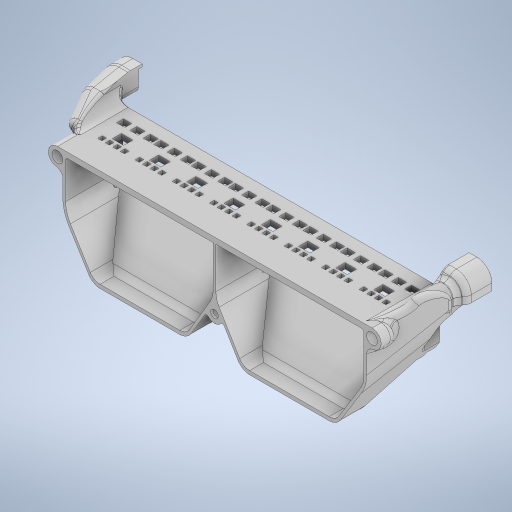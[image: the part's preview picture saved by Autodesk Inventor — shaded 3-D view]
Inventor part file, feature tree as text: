
AUTODESK INVENTOR PART (.ipt)
format: ipt  version: 2023.1 (Build 271208000, 208)  size: 8,087,552 bytes
history: native  units: mm
features: delete_face x74, projected_geometry x69, reference x62, sketch x58, extrude x56, fillet x51, other x19, chamfer x18, move_body x14, direct_edit x12, hole x3, plane x2
ambient origin geometry x8: Origin, YZ Plane, XZ Plane, XY Plane, X Axis, Y Axis, Z Axis, Center Point
bodies: Volumenkörper1 (feature_tree)
feature tree (438):
  extrude  "Extrusion1"  Depth=2.6mm
  extrude  "Extrusion2"  Depth=0.4195mm
  extrude  "Extrusion3"  Depth=8.0mm
  extrude  "Extrusion4"  Depth=2.6mm
  extrude  "Extrusion5"  Depth=0.482959mm
  extrude  "Extrusion6"  Depth=0.4mm
  delete_face  "Fläche löschen1"
  extrude  "Extrusion7"  Depth=9.8mm TaperAngle=0.0deg
  extrude  "Extrusion8"  Depth=3.0mm TaperAngle=0.0deg
  extrude  "Extrusion9"  Depth=40.0mm
  delete_face  "Fläche löschen2"
  delete_face  "Fläche löschen3"
  delete_face  "Fläche löschen4"
  extrude  "Extrusion10"  Depth=40.0mm
  delete_face  "Fläche löschen5"
  delete_face  "Fläche löschen6"
  delete_face  "Fläche löschen7"
  extrude  "Extrusion11"  Depth=12.004mm
  delete_face  "Fläche löschen8"
  extrude  "Extrusion12"  Depth=12.131mm
  delete_face  "Fläche löschen9"
  delete_face  "Fläche löschen10"
  delete_face  "Fläche löschen11"
  delete_face  "Fläche löschen12"
  extrude  "Extrusion13"  Depth=2.0mm
  extrude  "Extrusion14"  Depth=12.0mm TaperAngle=0.0deg
  delete_face  "Fläche löschen13"
  direct_edit  "Direktbearbeitung1"
  extrude  "Extrusion15"  Depth=0.2mm
  extrude  "Extrusion16"  Depth=0.2mm
  chamfer  "Fase1"  Distance=12.0mm
  delete_face  "Fläche löschen14"
  delete_face  "Fläche löschen15"
  chamfer  "Fase2"  Distance=10.0mm
  delete_face  "Fläche löschen16"
  chamfer  "Fase3"  Distance=10.0mm
  chamfer  "Fase4"  [1 undecoded]
  extrude  "Extrusion17"  Depth=10.0mm TaperAngle=0.0deg
  extrude  "Extrusion18"  Depth=1.2mm
  delete_face  "Fläche löschen17"
  extrude  "Extrusion19"  Depth=54.3755mm
  delete_face  "Fläche löschen18"
  delete_face  "Fläche löschen19"
  extrude  "Extrusion20"  Depth=10.0mm TaperAngle=0.0deg
  extrude  "Extrusion21"  Depth=10.0mm
  fillet  "Rundung1"  Radius=2.044525mm
  fillet  "Rundung2"  Radius=2.044525mm
  delete_face  "Fläche löschen20"
  delete_face  "Fläche löschen21"
  extrude  "Extrusion22"  Depth=10.0mm TaperAngle=0.0deg
  delete_face  "Fläche löschen22"
  extrude  "Extrusion23"  Depth=40.4mm
  extrude  "Extrusion24"  Depth=40.4mm
  delete_face  "Fläche löschen23"
  extrude  "Extrusion25"  Depth=2.391982mm
  delete_face  "Fläche löschen24"
  extrude  "Extrusion26"  Depth=20.0mm
  delete_face  "Fläche löschen25"
  extrude  "Extrusion27"  TaperAngle=30.0deg  [1 undecoded]
  delete_face  "Fläche löschen26"
  direct_edit  "Direktbearbeitung2"
  extrude  "Extrusion28"  Depth=40.6558mm
  extrude  "Extrusion29"  Depth=4.1mm
  extrude  "Extrusion30"  Depth=4.1mm
  extrude  "Extrusion31"  Depth=11.1mm
  extrude  "Extrusion32"  Depth=12.3mm
  extrude  "Extrusion33"  Depth=16.4mm
  direct_edit  "Direktbearbeitung3"
  delete_face  "Fläche löschen27"
  extrude  "Extrusion34"  Depth=8.2mm
  delete_face  "Fläche löschen28"
  delete_face  "Fläche löschen29"
  delete_face  "Fläche löschen30"
  delete_face  "Fläche löschen31"
  fillet  "Rundung3"  Radius=7.0mm
  extrude  "Extrusion35"  Depth=1.2mm
  chamfer  "Fase5"  Distance=19.7279mm
  extrude  "Extrusion36"  Depth=3.0mm
  delete_face  "Fläche löschen32"
  delete_face  "Fläche löschen33"
  direct_edit  "Direktbearbeitung4"
  extrude  "Extrusion37"  Depth=3.0mm
  fillet  "Rundung4"  Radius=11.1mm
  fillet  "Rundung5"  Radius=4.1mm
  fillet  "Rundung6"  Radius=2.9mm
  fillet  "Rundung7"  Radius=4.1mm
  fillet  "Rundung8"  Radius=5.3mm
  fillet  "Rundung9"  Radius=12.3mm
  chamfer  "Fase7"  Distance=13.5mm
  extrude  "Extrusion38"  Depth=3.0mm
  sketch  "Skizze44"  dims[d78=10.0mm d79=0.0mm d80=10.0mm d81=0.0mm]
  extrude  "Extrusion39"  Depth=3.0mm
  extrude  "Extrusion40"  Depth=3.0mm
  direct_edit  "Direktbearbeitung5"
  chamfer  "Fase8"  Distance=15.2mm
  fillet  "Rundung10"  Radius=8.2mm
  delete_face  "Fläche löschen34"
  delete_face  "Fläche löschen35"
  fillet  "Rundung11"  Radius=7.0mm
  fillet  "Rundung12"  Radius=0.0mm
  extrude  "Extrusion41"  Depth=3.0mm
  extrude  "Extrusion42"  Depth=3.0mm
  direct_edit  "Direktbearbeitung6"
  hole  "Bohrung1"  [1 undecoded]
  direct_edit  "Direktbearbeitung7"
  extrude  "Extrusion43"  Depth=3.0mm
  fillet  "Rundung13"  Radius=17.6mm
  extrude  "Extrusion44"  Depth=3.0mm
  plane  "Arbeitsebene4"
  other  "Trennen2"
  fillet  "Rundung14"  Radius=13.5mm
  delete_face  "Fläche löschen37"
  fillet  "Rundung15"  Radius=11.1mm
  fillet  "Rundung16"  Radius=12.3mm
  extrude  "Extrusion45"  Depth=3.0mm
  hole  "Bohrung2"  [1 undecoded]
  fillet  "Rundung17"  Radius=4.1mm
  extrude  "Extrusion46"  Depth=3.0mm
  delete_face  "Fläche löschen38"
  fillet  "Rundung18"  Radius=0.0mm
  fillet  "Rundung19"  Radius=1.2mm
  fillet  "Rundung20"  Radius=4.1mm
  delete_face  "Fläche löschen39"
  fillet  "Rundung21"  Radius=2.9mm
  delete_face  "Fläche löschen40"
  fillet  "Rundung22"  Radius=1.2mm
  fillet  "Rundung23"  Radius=5.3mm
  fillet  "Rundung24"  Radius=0.0mm
  fillet  "Rundung25"  Radius=4.1mm
  delete_face  "Fläche löschen41"
  chamfer  "Fase9"  Distance=8.2mm
  delete_face  "Fläche löschen42"
  fillet  "Rundung26"  Radius=12.3mm
  delete_face  "Fläche löschen43"
  extrude  "Extrusion47"  Depth=3.0mm
  delete_face  "Fläche löschen44"
  delete_face  "Fläche löschen45"
  extrude  "Extrusion48"  Depth=3.0mm
  delete_face  "Fläche löschen46"
  chamfer  "Fase10"  Distance=5.3mm
  fillet  "Rundung27"  Radius=9.4mm
  fillet  "Rundung28"  Radius=13.5mm
  fillet  "Rundung29"  Radius=17.6mm
  delete_face  "Fläche löschen47"
  chamfer  "Fase11"  Distance=4.1mm
  delete_face  "Fläche löschen48"
  chamfer  "Fase12"  Distance=8.2mm
  extrude  "Extrusion49"  Depth=3.0mm
  fillet  "Rundung30"  Radius=16.4mm
  extrude  "Extrusion50"  Depth=3.0mm
  fillet  "Rundung31"  Radius=5.3mm
  fillet  "Rundung32"  Radius=9.4mm
  delete_face  "Fläche löschen49"
  delete_face  "Fläche löschen50"
  direct_edit  "Direktbearbeitung8"
  extrude  "Extrusion51"  Depth=3.0mm
  delete_face  "Fläche löschen51"
  delete_face  "Fläche löschen52"
  extrude  "Extrusion52"  Depth=3.0mm
  delete_face  "Fläche löschen53"
  delete_face  "Fläche löschen54"
  delete_face  "Fläche löschen55"
  delete_face  "Fläche löschen56"
  direct_edit  "Direktbearbeitung9"
  fillet  "Rundung40"  Radius=21.7mm
  chamfer  "Fase13"  Distance=12.3mm
  chamfer  "Fase14"  Distance=16.4mm
  chamfer  "Fase15"  Distance=20.5mm
  fillet  "Rundung41"  Radius=24.6mm
  fillet  "Rundung42"  Radius=28.7mm
  delete_face  "Fläche löschen57"
  direct_edit  "Direktbearbeitung10"
  delete_face  "Fläche löschen58"
  fillet  "Rundung43"  Radius=13.5mm
  fillet  "Rundung44"  Radius=17.6mm
  delete_face  "Fläche löschen59"
  fillet  "Rundung45"  Radius=21.7mm
  delete_face  "Fläche löschen60"
  fillet  "Rundung46"  Radius=25.8mm
  delete_face  "Fläche löschen61"
  delete_face  "Fläche löschen62"
  delete_face  "Fläche löschen63"
  hole  "Bohrung3"  [1 undecoded]
  fillet  "Rundung47"  Radius=16.4mm
  fillet  "Rundung48"  Radius=20.5mm
  fillet  "Rundung49"  Radius=24.6mm
  fillet  "Rundung50"  Radius=28.7mm
  delete_face  "Fläche löschen64"
  plane  "Arbeitsebene5"
  extrude  "Extrusion53"  Depth=3.0mm
  direct_edit  "Direktbearbeitung11"
  fillet  "Rundung51"  Radius=17.6mm
  chamfer  "Fase16"  Distance=21.7mm
  delete_face  "Fläche löschen65"
  delete_face  "Fläche löschen66"
  extrude  "Extrusion54"  Depth=3.0mm
  delete_face  "Fläche löschen67"
  fillet  "Rundung52"  Radius=29.9mm
  extrude  "Extrusion55"  Depth=3.0mm
  fillet  "Rundung53"  Radius=28.7mm
  delete_face  "Fläche löschen68"
  extrude  "Extrusion56"  Depth=3.0mm
  fillet  "Rundung54"  Radius=36.9mm
  fillet  "Rundung55"  Radius=29.9mm
  chamfer  "Fase17"  Distance=34.0mm
  delete_face  "Fläche löschen69"
  delete_face  "Fläche löschen70"
  delete_face  "Fläche löschen71"
  direct_edit  "Direktbearbeitung12"
  delete_face  "Fläche löschen72"
  fillet  "Rundung56"  Radius=4.1mm
  chamfer  "Fase18"  Distance=1.2mm
  delete_face  "Fläche löschen73"
  chamfer  "Fase19"  Distance=2.9mm
  fillet  "Rundung57"  Radius=5.3mm
  fillet  "Rundung58"  Radius=12.3mm
  delete_face  "Fläche löschen74"
  delete_face  "Fläche löschen75"
  sketch  "Skizze1"  dims[d0=8.8mm d1=0.0mm d4=2.6mm]
  reference  "Referenz1"
  reference  "Referenz2"
  reference  "Referenz3"
  reference  "Referenz4"
  reference  "Referenz5"
  reference  "Referenz6"
  reference  "Referenz7"
  reference  "Referenz8"
  reference  "Referenz9"
  reference  "Referenz10"
  reference  "Referenz11"
  reference  "Referenz12"
  reference  "Referenz13"
  sketch  "Skizze2"  dims[d5=0.4195mm d6=0.4195mm]
  reference  "Referenz14"
  reference  "Referenz15"
  projected_geometry  "Projizierte Kontur1"
  reference  "Referenz16"
  reference  "Referenz17"
  reference  "Referenz18"
  reference  "Referenz19"
  sketch  "Skizze3"  dims[d7=5.999988mm d8=8.0mm]
  projected_geometry  "Projizierte Kontur2"
  reference  "Referenz20"
  reference  "Referenz21"
  reference  "Referenz22"
  reference  "Referenz23"
  reference  "Referenz24"
  reference  "Referenz25"
  sketch  "Skizze4"  dims[d9=8.0mm d10=2.6mm]
  projected_geometry  "Projizierte Kontur3"
  reference  "Referenz26"
  reference  "Referenz27"
  reference  "Referenz28"
  reference  "Referenz29"
  sketch  "Skizze5"  dims[d11=0.482959mm d12=0.482959mm]
  projected_geometry  "Projizierte Kontur4"
  projected_geometry  "Projizierte Kontur5"
  projected_geometry  "Projizierte Kontur6"
  projected_geometry  "Projizierte Kontur7"
  sketch  "Skizze7"  dims[d13=0.4mm d14=0.4mm]
  projected_geometry  "Projizierte Kontur8"
  reference  "Referenz30"
  reference  "Referenz31"
  sketch  "Skizze9"  dims[d15=2.6mm d16=9.8mm d17=0.0mm]
  projected_geometry  "Projizierte Kontur9"
  reference  "Referenz34"
  reference  "Referenz35"
  reference  "Referenz36"
  sketch  "Skizze10"  dims[d18=0.4mm d19=3.0mm d20=0.0mm]
  projected_geometry  "Projizierte Kontur10"
  projected_geometry  "Projizierte Kontur11"
  sketch  "Skizze11"  dims[d21=40.0mm d22=40.0mm]
  projected_geometry  "Projizierte Kontur12"
  sketch  "Skizze13"  dims[d23=40.0mm d24=40.0mm]
  projected_geometry  "Projizierte Kontur13"
  sketch  "Skizze14"  dims[d25=12.004mm d26=12.004mm]
  projected_geometry  "Projizierte Kontur14"
  reference  "Referenz37"
  reference  "Referenz38"
  reference  "Referenz39"
  reference  "Referenz40"
  sketch  "Skizze15"  dims[d27=12.131mm d28=12.131mm]
  projected_geometry  "Projizierte Kontur15"
  sketch  "Skizze16"  dims[d29=2.0mm d30=0.492mm]
  projected_geometry  "Projizierte Kontur16"
  projected_geometry  "Projizierte Kontur17"
  sketch  "Skizze17"  dims[d31=0.492mm d32=12.0mm d33=0.0mm]
  projected_geometry  "Projizierte Kontur18"
  reference  "Referenz41"
  reference  "Referenz42"
  reference  "Referenz43"
  reference  "Referenz44"
  reference  "Referenz45"
  sketch  "Skizze18"  dims[d34=0.2mm d35=0.2mm]
  projected_geometry  "Projizierte Kontur19"
  sketch  "Skizze20"  dims[d36=0.2mm d37=0.2mm]
  projected_geometry  "Projizierte Kontur20"
  projected_geometry  "Projizierte Kontur21"
  sketch  "Skizze21"  dims[d38=0.2mm]
  sketch  "Skizze22"  dims[d39=0.2mm]
  projected_geometry  "Projizierte Kontur22"
  projected_geometry  "Projizierte Kontur23"
  sketch  "Skizze23"  dims[d40=0.2mm]
  sketch  "Skizze24"  dims[d41=1.6mm]
  projected_geometry  "Projizierte Kontur24"
  sketch  "Skizze25"  dims[d42=1.6mm]
  projected_geometry  "Projizierte Kontur25"
  projected_geometry  "Projizierte Kontur26"
  sketch  "Skizze27"  dims[d43=1.6mm]
  projected_geometry  "Projizierte Kontur28"
  sketch  "Skizze28"  dims[d44=1.6mm]
  projected_geometry  "Projizierte Kontur29"
  projected_geometry  "Projizierte Kontur30"
  projected_geometry  "Projizierte Kontur31"
  sketch  "Skizze29"  dims[d45=1.6mm]
  projected_geometry  "Projizierte Kontur32"
  sketch  "Skizze30"  dims[d46=1.6mm]
  projected_geometry  "Projizierte Kontur33"
  sketch  "Skizze31"  dims[d47=1.6mm]
  projected_geometry  "Projizierte Kontur34"
  sketch  "Skizze32"  dims[d48=1.6mm d49=12.0mm d50=0.0mm]
  sketch  "Skizze33"  dims[d51=1.0mm]
  projected_geometry  "Projizierte Kontur35"
  sketch  "Skizze34"  dims[d52=4.2mm]
  projected_geometry  "Projizierte Kontur36"
  projected_geometry  "Projizierte Kontur37"
  sketch  "Skizze35"  dims[d53=1.2mm d54=10.0mm d55=0.0mm]
  projected_geometry  "Projizierte Kontur38"
  projected_geometry  "Projizierte Kontur39"
  sketch  "Skizze36"  dims[d61=1.6mm]
  projected_geometry  "Projizierte Kontur40"
  sketch  "Skizze37"  dims[d62=0.292mm]
  projected_geometry  "Projizierte Kontur41"
  projected_geometry  "Projizierte Kontur42"
  sketch  "Skizze38"  dims[d63=0.292mm]
  projected_geometry  "Projizierte Kontur43"
  sketch  "Skizze39"  dims[d64=1.2mm]
  projected_geometry  "Projizierte Kontur44"
  projected_geometry  "Projizierte Kontur45"
  sketch  "Skizze40"  dims[d65=1.2mm d66=10.0mm d67=0.0mm d68=0.0mm d69=0.0mm]
  projected_geometry  "Projizierte Kontur46"
  sketch  "Skizze41"  dims[d70=10.0mm d71=0.0mm d72=10.0mm d73=0.0mm]
  projected_geometry  "Projizierte Kontur47"
  sketch  "Skizze42"  dims[d74=0.0mm d75=1.2mm]
  projected_geometry  "Projizierte Kontur48"
  sketch  "Skizze43"  dims[d76=108.751mm d77=54.3755mm]
  projected_geometry  "Projizierte Kontur49"
  reference  "Referenz47"
  reference  "Referenz48"
  reference  "Referenz49"
  reference  "Referenz50"
  reference  "Referenz51"
  reference  "Referenz52"
  reference  "Referenz53"
  reference  "Referenz54"
  reference  "Referenz55"
  reference  "Referenz56"
  reference  "Referenz57"
  reference  "Referenz58"
  reference  "Referenz59"
  reference  "Referenz60"
  reference  "Referenz61"
  reference  "Referenz62"
  reference  "Referenz63"
  sketch  "Skizze45"  dims[d82=10.0mm d83=0.0mm d84=1.2mm d85=2.044525mm d86=2.044525mm]
  projected_geometry  "Projizierte Kontur50"
  projected_geometry  "Projizierte Kontur51"
  sketch  "Skizze46"  dims[d87=10.0mm d88=0.0mm d89=0.0mm d90=0.0mm d91=5.0mm]
  projected_geometry  "Projizierte Kontur52"
  sketch  "Skizze47"  dims[d92=12.0mm d93=0.0mm d94=40.4mm]
  reference  "Referenz64"
  reference  "Referenz65"
  sketch  "Skizze48"  dims[d95=40.4mm d97=40.4mm]
  sketch  "Skizze49"  dims[d98=0.0mm d99=2.391982mm]
  sketch  "Skizze50"  dims[d100=2.6mm d101=20.0mm]
  projected_geometry  "Projizierte Kontur53"
  sketch  "Skizze51"  dims[d102=30.0deg d103=30.0deg]
  projected_geometry  "Projizierte Kontur54"
  sketch  "Skizze52"  dims[d104=45.0deg d105=40.6558mm]
  projected_geometry  "Projizierte Kontur55"
  projected_geometry  "Projizierte Kontur56"
  projected_geometry  "Projizierte Kontur57"
  sketch  "Skizze53"  dims[d106=1.2mm d107=4.1mm]
  projected_geometry  "Projizierte Kontur58"
  projected_geometry  "Projizierte Kontur59"
  sketch  "Skizze54"  dims[d108=2.9mm d109=4.1mm]
  projected_geometry  "Projizierte Kontur60"
  projected_geometry  "Projizierte Kontur61"
  sketch  "Skizze55"  dims[d110=5.3mm d111=11.1mm]
  projected_geometry  "Projizierte Kontur62"
  sketch  "Skizze56"  dims[d112=12.3mm d113=12.3mm]
  projected_geometry  "Projizierte Kontur63"
  sketch  "Skizze57"  dims[d114=13.5mm d115=16.4mm]
  projected_geometry  "Projizierte Kontur64"
  projected_geometry  "Projizierte Kontur65"
  sketch  "Skizze58"  dims[d116=15.2mm d117=8.2mm d118=7.0mm]
  projected_geometry  "Projizierte Kontur66"
  sketch  "Skizze59"  dims[d119=0.0mm d120=1.2mm]
  projected_geometry  "Projizierte Kontur67"
  sketch  "Skizze60"  dims[d121=8.2mm]
  projected_geometry  "Projizierte Kontur68"
  sketch  "Skizze61"  dims[d122=9.4mm]
  projected_geometry  "Projizierte Kontur69"
  sketch  "Skizze62"  dims[d123=16.4mm]
  sketch  "Skizze63"  dims[d124=17.6mm d125=19.7279mm d126=19.3mm d127=12.3mm d128=11.1mm d129=4.1mm d130=2.9mm d131=4.1mm d132=5.3mm d133=12.3mm d134=13.5mm d135=20.5mm d136=20.9279mm d137=16.4mm d138=15.2mm d139=8.2mm d140=7.0mm d141=0.0mm d142=1.2mm d143=8.2mm d144=9.4mm d145=16.4mm d146=17.6mm d147=12.3mm d148=13.5mm d149=11.1mm d150=12.3mm d151=4.1mm d152=2.9mm d153=4.1mm d154=5.3mm d155=0.0mm d156=1.2mm d157=4.1mm d158=2.9mm d159=1.2mm d160=5.3mm d161=0.0mm d162=4.1mm d163=8.2mm d164=12.3mm d165=16.4mm d166=1.2mm d167=5.3mm d168=9.4mm d169=13.5mm d170=17.6mm d171=4.1mm d172=8.2mm d173=12.3mm d174=16.4mm d175=20.5mm d176=5.3mm d177=9.4mm d178=13.5mm d179=17.6mm d180=21.7mm d181=12.3mm d182=16.4mm d183=20.5mm d184=24.6mm d185=28.7mm d186=13.5mm d187=17.6mm d188=21.7mm d189=25.8mm d190=29.9mm d191=16.4mm d192=20.5mm d193=24.6mm d194=28.7mm d195=32.8mm d196=17.6mm d197=21.7mm d198=25.8mm d199=29.9mm d200=34.0mm d201=28.7mm d202=32.8mm d203=36.9mm d204=29.9mm d205=34.0mm d206=4.1mm d207=1.2mm d208=2.9mm d209=5.3mm d210=12.3mm d211=8.2mm d212=4.1mm d213=0.0mm d214=16.4mm d215=13.5mm d216=9.4mm d217=5.3mm d218=1.2mm d219=17.6mm d220=4.1mm d221=20.5mm d222=16.4mm d223=12.3mm d224=8.2mm d225=5.3mm d226=21.7mm d227=17.6mm d228=13.5mm d229=9.4mm d230=24.6mm d231=20.5mm d232=16.4mm d233=12.3mm d234=28.7mm d235=25.8mm d236=21.7mm d237=17.6mm d238=13.5mm d239=29.9mm d240=16.4mm d241=32.8mm d242=28.7mm d243=24.6mm d244=20.5mm d245=17.6mm d246=34.0mm d247=29.9mm d248=25.8mm d249=21.7mm d250=28.7mm d251=36.9mm d252=32.8mm d253=29.9mm d254=34.0mm d255=3.592392mm d256=0.0mm d257=3.592392mm d258=3.592392mm d259=0.0mm d260=3.592392mm d261=9.572437mm d262=8.363481mm d263=0.10481mm d264=25.260409mm d265=0.336902mm d266=0.336902mm d267=4.2624mm d268=15.4655mm d269=4.2624mm d270=16.6655mm d271=33.794072mm d272=33.794072mm d273=36.334277mm d274=36.334277mm d275=38.3558mm d276=18.6279mm d277=0.1279mm d278=0.1279mm d279=1.2mm d280=0.6mm d281=2.0mm d282=0.0mm d283=0.6mm d284=2.0mm d285=45.0deg d286=0.4mm d287=2.0mm d288=45.0deg d289=0.6mm d290=2.0mm d291=45.0deg d292=0.4mm d293=2.0mm d294=45.0deg d295=0.0mm d296=0.0mm d297=10.0mm d298=0.0mm d300=12.0mm d301=1.2mm d302=10.0mm d303=0.0mm d304=0.0mm d305=0.0mm d306=3.0mm d307=0.0mm d308=5.0mm d309=6.6mm d310=3.0mm d311=0.0mm d312=10.0mm d313=0.0mm d314=10.0mm d315=0.0mm d316=10.0mm d317=0.0mm d318=0.0mm d319=0.0mm d320=10.0mm d321=0.0mm d322=0.0mm d323=0.0mm d324=5.0mm d325=10.0mm d326=0.0mm d327=10.0mm d328=0.0mm d329=10.0mm d330=0.0mm d331=10.0mm d332=0.0mm d333=1.2mm d334=10.0mm d335=0.0mm d336=10.0mm d337=0.0mm d338=0.0mm d339=0.0mm d340=1.75mm d341=10.0mm d342=0.0mm d343=0.4mm d344=2.0mm d345=0.0mm d346=0.6mm d347=2.0mm d348=45.0deg d349=1.0mm d350=0.0mm d351=0.0mm d352=0.0mm d353=1.75mm d354=1.0mm d355=0.0mm d356=2.0mm d357=1.0mm d358=0.4mm d359=10.0mm d360=5.0mm d361=2.0mm d365=0.4mm d366=2.0mm d367=45.0deg d368=5.6mm d369=3.0mm d370=3.6mm d371=3.6mm d372=3.6mm d373=2.220006mm d374=2.220006mm d375=3.6mm d376=3.6mm d377=3.6mm d378=2.220006mm d379=2.220006mm d380=3.6mm d381=3.6mm d382=3.6mm d383=2.220006mm d384=2.220006mm d385=3.6mm d386=3.6mm d387=3.6mm d388=2.220006mm d389=2.220006mm d390=3.6mm d391=3.6mm d392=3.6mm d393=2.220006mm d394=2.220006mm d395=3.6mm d396=3.6mm d397=3.6mm d398=2.220006mm d399=2.220006mm d400=3.6mm d401=3.6mm d402=3.6mm d403=2.220006mm d404=2.220006mm d425=3.6mm d426=3.6mm d427=3.6mm d428=2.220006mm d429=2.220006mm d430=0.4mm d431=0.0mm d432=0.3mm d433=0.3mm d434=0.3mm d435=0.3mm d437=0.3mm d438=1.2mm d439=1.2mm d440=1.2mm d441=1.2mm d443=1.2mm d444=10.0mm d445=0.0mm d446=1.6mm d447=0.0mm d448=0.0mm d449=0.0mm d450=4.0mm d451=3.8mm d452=2.0mm d453=45.0deg d454=4.0mm d455=4.0mm d456=5.2mm d457=5.0mm d458=10.0mm d459=0.0mm d460=6.2mm d461=0.0mm d462=0.0mm d463=0.0mm d464=0.0mm d465=-1.0mm d466=3.3mm d467=6.0mm d468=4.7mm d469=5.0mm d470=90.0deg d471=8.0mm d472=20.594885mm d473=0.0mm d474=0.0mm d475=0.4mm d476=0.0mm d477=0.0mm d478=1.485505mm d479=0.0mm d480=0.0mm d481=1.000006mm d482=0.0mm d483=0.0mm d484=10.0mm d485=3.0mm d486=3.0mm d487=4.0mm d488=5.0mm d489=5.0mm d490=5.0mm d491=5.0mm d492=5.0mm d493=5.0mm d494=5.0mm d495=5.0mm d496=5.120006mm d497=5.120006mm d498=5.120006mm d499=5.120006mm d500=5.120006mm d501=5.120006mm d502=5.120006mm d503=5.120006mm d504=5.120006mm d505=5.120006mm d506=5.120006mm d507=5.120006mm d508=5.120006mm d509=5.120006mm d510=5.120006mm d511=5.120006mm d512=1.0mm d513=2.0mm d514=2.0mm d522=1.8mm d523=2.0mm d524=1.8mm d525=1.8mm d526=1.8mm d527=11.640012mm d528=11.640012mm d529=1.480004mm d530=1.480004mm d531=1.480004mm d532=1.8mm d533=2.0mm d534=1.8mm d535=1.8mm d536=1.8mm d537=11.640012mm d538=1.480004mm d539=1.480004mm d540=1.480004mm d541=2.0mm d542=11.640012mm d543=1.8mm d544=2.0mm d545=1.8mm d546=1.8mm d547=1.8mm d548=11.640012mm d549=1.480004mm d550=1.480004mm d551=1.480004mm d552=2.0mm d553=11.640012mm d554=1.8mm d555=2.0mm d556=1.8mm d557=1.8mm d558=1.8mm d559=11.640012mm d560=1.480004mm d561=1.480004mm d562=1.480004mm d563=2.0mm d564=11.640012mm d565=1.8mm d566=2.0mm d567=1.8mm d568=1.8mm d569=1.8mm d570=11.640012mm d571=1.480004mm d572=1.480004mm d573=1.480004mm d574=2.0mm d575=11.640012mm d576=1.8mm d577=2.0mm d578=1.8mm d579=1.8mm d580=1.8mm d581=11.640012mm d582=1.480004mm d583=1.480004mm d584=1.480004mm d585=2.0mm d586=11.640012mm d587=1.8mm d588=2.0mm d589=1.8mm d590=1.8mm d591=1.8mm d592=11.640012mm d593=1.480004mm d594=1.480004mm d595=1.480004mm d596=2.0mm d597=11.640012mm d598=1.8mm d599=2.0mm d600=1.8mm d601=1.8mm d602=1.8mm d603=11.640012mm d604=1.480004mm d605=1.480004mm d606=1.480004mm d607=2.0mm d608=11.640012mm d609=3.0mm d610=0.0mm d611=-6.0mm d612=10.0mm d613=10.0mm d614=14.0mm d615=4.7mm d616=6.0mm d617=0.0mm d618=3.3mm d619=6.0mm d620=4.7mm d621=5.0mm d622=90.0deg d623=8.0mm d624=20.594885mm d625=1.0mm d626=1.2mm d627=1.2mm d628=0.0mm d629=0.0mm d630=10.0mm d631=10.0mm d632=5.0mm d633=1.0mm d634=1.0mm d635=10.0mm d636=10.0mm d637=3.0mm d638=0.4mm d639=2.0mm d640=45.0deg d641=2.0mm d642=10.0mm d643=0.0mm d644=10.0mm d645=0.0mm d646=0.4mm d647=2.0mm d648=45.0deg d649=1.0mm d650=8.0mm d651=1.0mm d652=0.4mm d653=2.0mm d654=45.0deg d655=0.4mm d656=2.0mm d657=45.0deg d658=0.0mm d659=0.0mm d660=2.0mm d661=4.7mm d662=4.7mm d663=1.6mm d664=1.6mm d665=7.0mm d666=0.0mm d667=3.0mm d668=3.0mm d669=0.0mm d670=0.0mm d671=1.1mm d672=15.0mm d673=0.0mm d674=0.0mm d675=0.0mm d683=0.0mm d684=0.0mm d685=10.0mm d686=2.0mm d687=6.25mm d688=2.0mm d689=45.0deg d690=8.75mm d691=2.0mm d692=45.0deg d693=6.0mm d694=2.0mm d695=45.0deg d696=6.0mm d697=4.0mm d698=0.0mm d699=0.0mm d700=3.0mm d701=4.0mm d702=3.0mm d703=3.0mm d704=1.25mm d705=3.3mm d706=6.0mm d707=4.7mm d708=5.0mm d709=90.0deg d710=6.0mm d711=20.594885mm d712=2.0mm d713=1.0mm d714=3.0mm d715=3.0mm d716=1.6mm d717=1.0mm d718=0.0mm d719=0.0mm d720=0.0mm d721=2.0mm d722=0.8mm d723=0.4mm d724=2.0mm d725=45.0deg d726=0.8mm d727=4.0mm d728=0.0mm d729=1.0mm d730=0.8mm d731=20.0mm d732=0.0mm d733=0.6mm d734=10.0mm d735=0.0mm d736=1.0mm d737=8.0mm d738=0.5mm d739=2.0mm d740=45.0deg d741=0.0mm d742=0.0mm d743=-0.2mm d744=2.0mm d745=0.7mm d746=2.0mm d747=45.0deg d748=1.0mm d749=2.0mm d750=45.0deg d751=3.0mm d752=0.4mm d677=0.0mm d678=0.0mm d679=0.0mm d680=0.0mm d681=0.0mm]
  projected_geometry  "Projizierte Kontur70"
  other  "<userpath>\Desktop\GitHub\Voron-2-Mods\Mix\Octopus_Pro_FanCase\FanCase_Assembly.iam"
  other  "FanCase_Assembly.iam"
  other  "Octopus_Pro - beta:1"
  other  "COMPONENTS"
  other  "M11"
  other  "M12"
  other  "BOARD_OUTLINE"
  other  "J47"
  other  "XH-4P"
  other  "MOTOR_DRIVER"
  other  "J15"
  other  "254-3X4-1"
  other  "J41"
  other  "IDC2X5P"
  parser-record x1  (decoder bookkeeping rows leaked as tree rows — omitted from the tree; the rows remain in map.json)
  other  "J67"
  other  "HB9500-8P"
  other  "J12"
  move_body  "Verschieben1"
  move_body  "Verschieben2"
  move_body  "Verschieben3"
  move_body  "Verschieben4"
  move_body  "Verschieben5"
  move_body  "Verschieben6"
  move_body  "Verschieben7"
  move_body  "Verschieben8"
  move_body  "Verschieben9"
  move_body  "Verschieben10"
  move_body  "Verschieben11"
  move_body  "Verschieben12"
  move_body  "Verschieben13"
  move_body  "Verschieben14"
note: 5 required parameter values undecoded (feature->parameter linkage not recoverable at this tier; creation-order binding heuristic only, values carry confidence <= 0.55)
